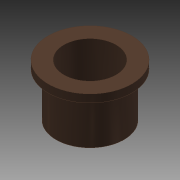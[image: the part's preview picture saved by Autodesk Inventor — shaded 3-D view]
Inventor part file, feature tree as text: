
AUTODESK INVENTOR PART (.ipt)
format: ipt  version: 2015 (Build 190159000, 159)  size: 108,544 bytes
history: native  units: in
note: dims shown in document units (in); Inventor stores cm internally (conversion verified against a paired STEP export)
features: revolve x1, sketch x1
ambient origin geometry x8: Origin, YZ Plane, XZ Plane, XY Plane, X Axis, Y Axis, Z Axis, Center Point
bodies: Solid1 (feature_tree)
feature tree (2):
  revolve  "Revolution1"  [1 undecoded]
  sketch  "Sketch1"  dims[d0=0.1969in d2=0.0591in d3=0.3937in d4=0.0591in d5=0.315in d6=90.0deg]
note: 1 required parameter value undecoded (feature->parameter linkage not recoverable at this tier; creation-order binding heuristic only, values carry confidence <= 0.55)
